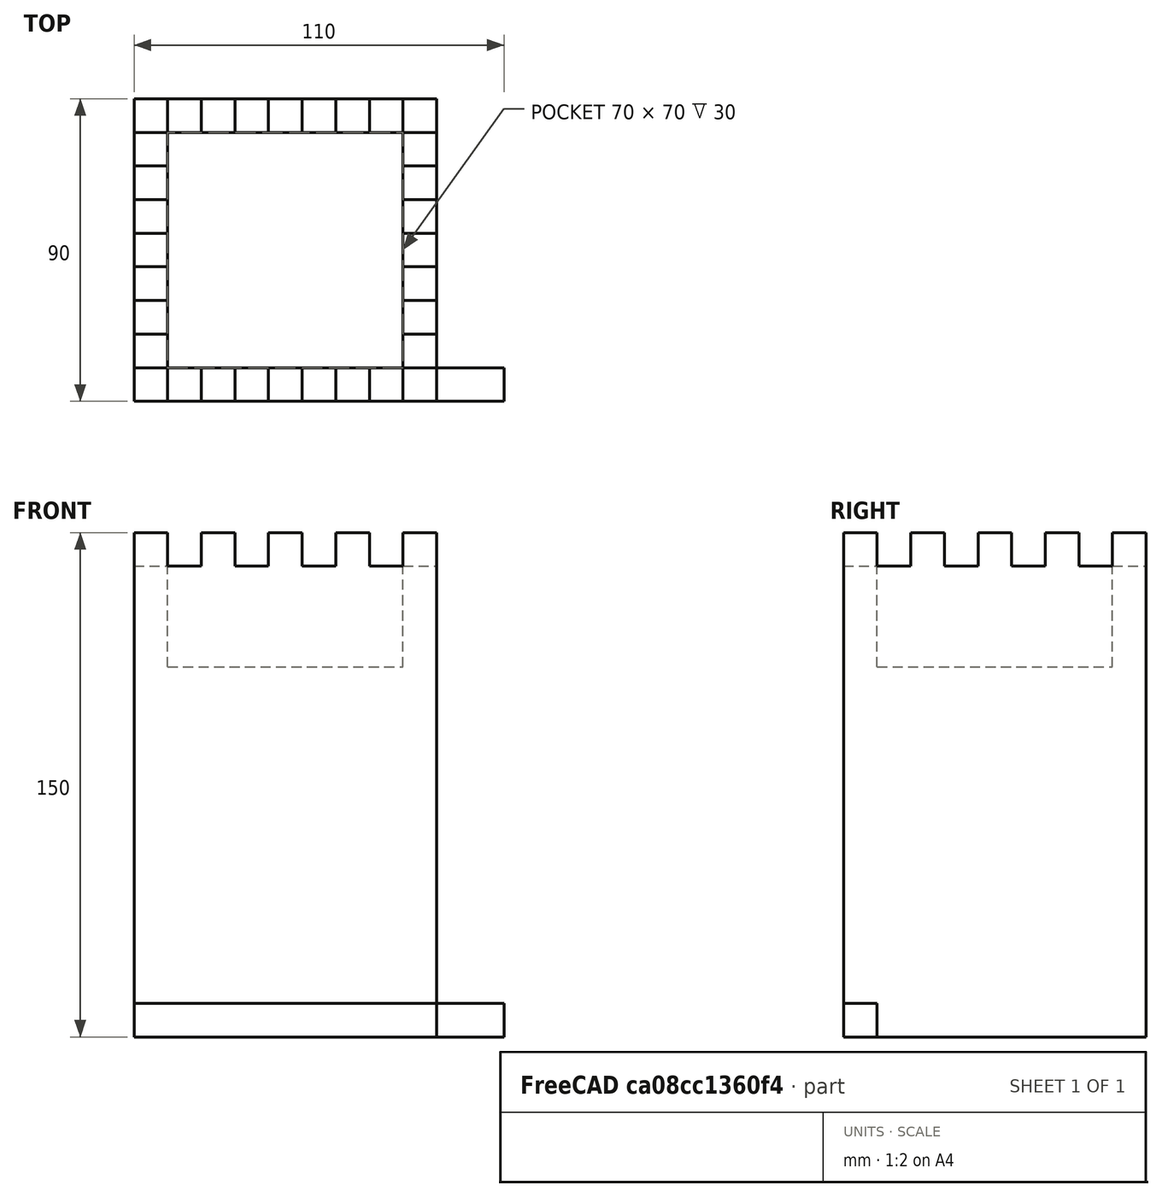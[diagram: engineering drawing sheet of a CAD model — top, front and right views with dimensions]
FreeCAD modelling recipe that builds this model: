
FCSTD DOCUMENT  (FreeCAD 0.21R33694 (Git))
Label: OJT1_T10R02_torre
License: All rights reserved
LicenseURL: https://en.wikipedia.org/wiki/All_rights_reserved
objects: Part::Box×4, Part::FeaturePython×2, Part::Cut×2, Part::MultiFuse×1
note: 7 computed .brp shape members not serialized (recipe doc carries the construction recipe); baked Part::Feature solids carry a one-line shape summary decoded from their .brp

FEATURE [Part::Box] Box  label="Cub"
  AttacherType = Attacher::AttachEngine3D
  Height = 150
  Length = 90
  Width = 90
FEATURE [Part::Box] Box003  label="Barra1"
  AttacherType = Attacher::AttachEngine3D
  Height = 10
  Length = 110
  Width = 10
FEATURE [Part::FeaturePython] Array  label="Barras_horitz"  # Draft array (typed FeaturePython)
  AlwaysSyncPlacement = false
  Angle = 360
  ArrayType = 0
  Axis = (0,0,1)
  Base = -> Box003
  Center = (0,0,0)
  Count = 4
  ExpandArray = false
  Fuse = false
  IntervalAxis = (0,0,0)
  IntervalX = (100,0,0)
  IntervalY = (0,20,0)
  IntervalZ = (0,0,100)
  NumberCircles = 3
  NumberPolar = 5
  NumberX = 1
  NumberY = 4
  NumberZ = 1
  Placement = pos=(-10,10,140) rot=(0,0,1;0rad)
  PlacementList = 4 placements: arithmetic series from (0,0,0) step (0,20,0) to (0,60,0)
  RadialDistance = 50
  ScaleList = (4) [(1,1,1),(1,1,1),(1,1,1),(1,1,1)]
  Symmetry = 1
  TangentialDistance = 25
FEATURE [Part::Box] Box004  label="Barra002"
  AttacherType = Attacher::AttachEngine3D
  Height = 10
  Length = 110
  Width = 10
FEATURE [Part::FeaturePython] Array001  label="Barras_vert"  # Draft array (typed FeaturePython)
  AlwaysSyncPlacement = false
  Angle = 360
  ArrayType = 0
  Axis = (0,0,1)
  Base = -> Box004
  Center = (0,0,0)
  Count = 4
  ExpandArray = false
  Fuse = false
  IntervalAxis = (0,0,0)
  IntervalX = (100,0,0)
  IntervalY = (0,20,0)
  IntervalZ = (0,0,100)
  NumberCircles = 3
  NumberPolar = 5
  NumberX = 1
  NumberY = 4
  NumberZ = 1
  Placement = pos=(80,-10,140) rot=(0,0,1;1.5708rad)
  PlacementList = 4 placements: arithmetic series from (0,0,0) step (0,20,0) to (0,60,0)
  RadialDistance = 50
  ScaleList = (4) [(1,1,1),(1,1,1),(1,1,1),(1,1,1)]
  Symmetry = 1
  TangentialDistance = 25
FEATURE [Part::MultiFuse] Fusion  label="Barres"
  Shapes = -> [Array,Array001]
FEATURE [Part::Box] Box002  label="Cub002"
  AttacherType = Attacher::AttachEngine3D
  Height = 110
  Length = 70
  Placement = pos=(10,10,110) rot=(0,0,1;0rad)
  Width = 70
FEATURE [Part::Cut] Cut  label="Torre001"
  Base = -> Box
  Tool = -> Box002
FEATURE [Part::Cut] Cut001  label="Castell"
  Base = -> Cut
  Tool = -> Fusion
